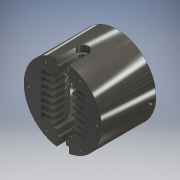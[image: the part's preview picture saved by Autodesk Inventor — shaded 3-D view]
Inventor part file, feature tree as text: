
AUTODESK INVENTOR PART (.ipt)
format: ipt  version: 2016 (Build 200138000, 138)  size: 500,736 bytes
history: native  units: mm
features: sketch x9, extrude x8, plane x4, projected_geometry x4, mirror x2, pattern_linear x2, loft x1, fillet x1, hole x1, pattern_circular x1, other x1
ambient origin geometry x8: Origin, YZ Plane, XZ Plane, XY Plane, X Axis, Y Axis, Z Axis, Center Point
bodies: Solid1 (feature_tree)
feature tree (34):
  sketch  "Sketch1"  dims[d0=100.0mm d1=70.0mm d2=0.0mm]
  extrude  "Extrusion1"  Depth=70.0mm TaperAngle=0.0deg
  extrude  "Extrusion2"  Depth=2.6mm
  sketch  "Sketch18"  dims[d3=35.0mm d4=50.0mm d5=50.0mm d6=0.0mm d7=0.0mm d71=2.6mm]
  plane  "Work Plane3"
  plane  "Work Plane4"
  extrude  "Extrusion11"  Depth=8.0mm
  loft  "Loft3"
  mirror  "Mirror1"
  extrude  "Extrusion12"  Depth=16.0mm
  extrude  "Extrusion13"  Depth=5.0mm
  pattern_linear  "Rectangular Pattern2"  Count1=5  [1 undecoded]
  extrude  "Extrusion14"  Depth=4.0mm TaperAngle=0.0deg
  pattern_linear  "Rectangular Pattern3"  Spacing1=0.0mm  [1 undecoded]
  fillet  "Fillet5"  [1 undecoded]
  hole  "Hole2"  [1 undecoded]
  pattern_circular  "Circular Pattern1"  [2 undecoded]
  extrude  "Extrusion15"  Depth=4.0mm
  plane  "Work Plane5"
  plane  "Work Plane6"
  extrude  "Extrusion16"  Depth=4.0mm TaperAngle=0.0deg
  mirror  "Mirror2"
  projected_geometry  "Projected Loop5"
  sketch  "Sketch22"  dims[d100=5.0mm d101=8.0mm]
  projected_geometry  "Projected Loop8"
  other  "Edges6"
  sketch  "Sketch23"  dims[d102=16.0mm d105=60.0deg]
  sketch  "Sketch24"  dims[d106=16.0mm d107=2.0mm]
  sketch  "Sketch25"  dims[d108=6.981317mm d109=5.0mm]
  sketch  "Sketch27"  dims[d110=35.0mm]
  sketch  "Sketch28"  dims[d111=15.0mm]
  projected_geometry  "Projected Loop9"
  sketch  "Sketch30"  dims[d112=5.0mm d117=50.0mm d118=70.0mm d119=20.0mm d120=0.0mm d121=0.0mm d122=90.0deg d123=0.0mm d124=90.0deg d125=20.0mm d126=0.0mm d127=5.5mm d128=55.0mm d129=20.0mm d130=0.0mm d131=26.5mm d132=70.0mm d134=8.0mm d136=45.0deg d137=6.0mm d138=1.6mm d139=0.0mm d140=30.0mm d142=10.0mm d143=10.0mm d144=6.0mm d145=4.2mm d146=6.0mm d147=4.0mm d148=2.0mm d149=90.0deg d150=8.0mm d151=20.594885mm d152=60.0mm d153=360.0deg d155=5.4mm d156=1600.0mm d157=0.0mm d158=4.2mm d159=4.0mm d160=0.0mm d161=7.0mm]
  projected_geometry  "Project Cut Edges3"
note: 6 required parameter values undecoded (feature->parameter linkage not recoverable at this tier; creation-order binding heuristic only, values carry confidence <= 0.55)
